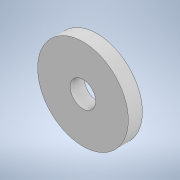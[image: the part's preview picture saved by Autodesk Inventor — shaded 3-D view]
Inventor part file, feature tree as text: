
AUTODESK INVENTOR PART (.ipt)
format: ipt  version: 2022 (Build 260153000, 153)  size: 136,704 bytes
history: native  units: in
note: dims shown in document units (in); Inventor stores cm internally (conversion verified against a paired STEP export)
features: extrude x1, sketch x1
ambient origin geometry x8: Origin, YZ Plane, XZ Plane, XY Plane, X Axis, Y Axis, Z Axis, Center Point
bodies: Body1 (feature_tree)
feature tree (2):
  extrude  "Extrusion1"  TaperAngle=0.0deg  [1 undecoded]
  sketch  "Sketch2"  dims[d0=0.1378in d1=0.0in]
note: 1 required parameter value undecoded (feature->parameter linkage not recoverable at this tier; creation-order binding heuristic only, values carry confidence <= 0.55)
